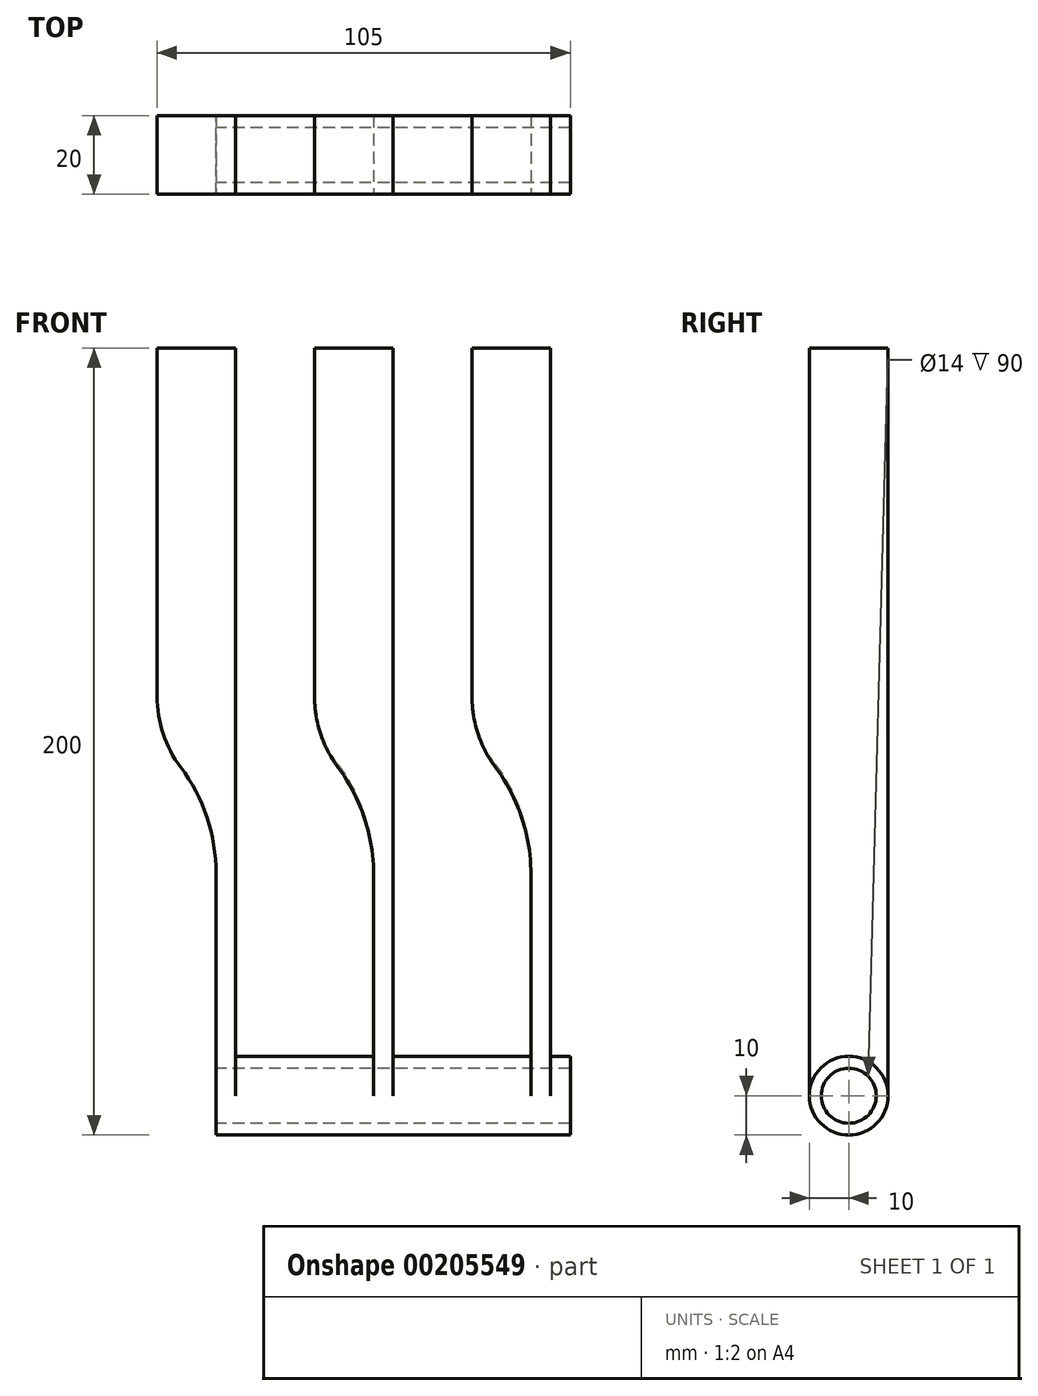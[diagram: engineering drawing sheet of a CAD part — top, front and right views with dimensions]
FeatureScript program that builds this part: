
annotation { "Feature Type Name" : "Feature", "Feature Type Description" : "" }
export const myFeature = defineFeature(function(context is Context, id is Id, definition is map)
    precondition{}
    {
        {
            assignVariable(context, id + "F0", {"name" : "width", "anyValue" : 120 * mm});
        }
        {
            var Q0;
            Q0=qCreatedBy(makeId("Front.planeOp"),FACE);
            var sketch = newSketch(context, id + "F1", { "sketchPlane" : qUnion([Q0])});
            skLineSegment(sketch, "E0.bottom", {"start": v(0, 0) * mm, "end": v(120, 0) * mm});
            skLineSegment(sketch, "E0.top", {"start": v(0, 200) * mm, "end": v(120, 200) * mm});
            skLineSegment(sketch, "E0.left", {"start": v(0, 0) * mm, "end": v(0, 200) * mm});
            skLineSegment(sketch, "E0.right", {"start": v(120, 0) * mm, "end": v(120, 200) * mm});
            skSolve(sketch);
        }
        {
            var Q0;
            Q0=qSketchRegion(id+"F1",true);
            extrude(context, id + "F2", {"entities" : qUnion([Q0]), "depth" : 1 / 6 * getVariable(context, 'width')});
        }
        {
            var Q0;
            Q0=makeQuery(id+"F2.opExtrude","SWEPT_FACE",FACE,{"disambiguationData":[OSD([sQuery(id+"F1.wireOp",EDGE,"E0.left")])]});
            var sketch = newSketch(context, id + "F3", { "sketchPlane" : qUnion([Q0])});
            skCircle(sketch, "E1", {"center": v(10, 10) * mm, "radius": 10 * mm});
            skPoint(sketch, "E1.centerSnap0", {"position": v(10, 0) * mm});
            skSolve(sketch);
        }
        {
            var Q0;
            {var subQ0=sQuery(id+"F3.wireOp",EDGE,"E1");var subQ1=sQuery(id+"F1.wireOp",EDGE,"E0.left");var subQ2=makeQuery(id+"F2.opExtrude","CAP_EDGE",EDGE,{"disambiguationData":[OSD([subQ1])],"isStart":false});var subQ3=makeQuery(id+"F3.imprint","INTERSECT",VERTEX,{"derivedFrom":[subQ2,subQ0]});Q0=makeQuery(id+"F3.imprint","IMPRINT",FACE,{"disambiguationData":[TD([[makeQuery(id+"F3.imprint","IMPRINT",EDGE,{"disambiguationData":[TD([[subQ3,1.0]])],"derivedFrom":subQ0}),-1.0]])]});}
            var Q1;
            {var subQ0=sQuery(id+"F3.wireOp",EDGE,"E1");var subQ1=sQuery(id+"F1.wireOp",EDGE,"E0.left");var subQ2=makeQuery(id+"F2.opExtrude","CAP_EDGE",EDGE,{"disambiguationData":[OSD([subQ1])],"isStart":true});var subQ3=makeQuery(id+"F3.imprint","INTERSECT",VERTEX,{"derivedFrom":[subQ2,subQ0]});Q1=makeQuery(id+"F3.imprint","IMPRINT",FACE,{"disambiguationData":[TD([[makeQuery(id+"F3.imprint","IMPRINT",EDGE,{"disambiguationData":[TD([[subQ3,-1.0]])],"derivedFrom":subQ0}),-1.0]])]});}
            var Q2;
            Q2=makeQuery(id+"F2.opExtrude","CAP_EDGE",EDGE,{"disambiguationData":[OSD([sQuery(id+"F1.wireOp",EDGE,"E0.bottom")])],"isStart":false});
            sweep(context, id + "F4", {"operationType" : NewBodyOperationType.REMOVE, "profiles" : qUnion([Q0, Q1]), "path" : qUnion([Q2])});
        }
        {
            var Q0;
            Q0=makeQuery(id+"F2.opExtrude","CAP_FACE",FACE,{"disambiguationData":[OSD([sQuery(id+"F1.wireOp",EDGE,"E0.bottom"),sQuery(id+"F1.wireOp",EDGE,"E0.top"),sQuery(id+"F1.wireOp",EDGE,"E0.left"),sQuery(id+"F1.wireOp",EDGE,"E0.right")])],"isStart":false});
            var sketch = newSketch(context, id + "F5", { "sketchPlane" : qUnion([Q0])});
            skLineSegment(sketch, "E2", {"start": v(60, 200) * mm, "end": v(60, 10) * mm});
            skLineSegment(sketch, "E3", {"start": v(20, 200) * mm, "end": v(20, 10) * mm});
            skLineSegment(sketch, "E4", {"start": v(40, 200) * mm, "end": v(40, 10) * mm});
            skLineSegment(sketch, "E5.MirrorCS", {"start": v(80, 200) * mm, "end": v(80, 10) * mm});
            skLineSegment(sketch, "E6.MirrorCS", {"start": v(100, 200) * mm, "end": v(100, 10) * mm});
            skSolve(sketch);
        }
        {
            var Q0;
            {var subQ0=sQuery(id+"F5.wireOp",EDGE,"E3");Q0=makeQuery(id+"F5.imprint","IMPRINT",FACE,{"disambiguationData":[TD([[makeQuery(id+"F5.imprint","IMPRINT",EDGE,{"derivedFrom":subQ0}),1.0]])]});}
            var Q1;
            {var subQ0=sQuery(id+"F5.wireOp",EDGE,"E2");Q1=makeQuery(id+"F5.imprint","IMPRINT",FACE,{"disambiguationData":[TD([[makeQuery(id+"F5.imprint","IMPRINT",EDGE,{"derivedFrom":subQ0}),1.0]])]});}
            var Q2;
            {var subQ0=sQuery(id+"F5.wireOp",EDGE,"E6.MirrorCS");Q2=makeQuery(id+"F5.imprint","IMPRINT",FACE,{"disambiguationData":[TD([[makeQuery(id+"F5.imprint","IMPRINT",EDGE,{"derivedFrom":subQ0}),1.0]])]});}
            var Q3;
            Q3=qConstructionFilter(qBodyType(qCreatedBy(id+"F3",EDGE),BodyType.WIRE),ConstructionObject.NO);
            sweep(context, id + "F6", {"operationType" : NewBodyOperationType.REMOVE, "profiles" : qUnion([Q0, Q1, Q2]), "path" : qUnion([Q3])});
        }
        {
            var Q0;
            Q0=makeQuery(id+"F2.opExtrude","SWEPT_FACE",FACE,{"disambiguationData":[OSD([sQuery(id+"F1.wireOp",EDGE,"E0.left")])]});
            var sketch = newSketch(context, id + "F7", { "sketchPlane" : qUnion([Q0])});
            skCircle(sketch, "E7", {"center": v(10, 10) * mm, "radius": 7 * mm});
            skSolve(sketch);
        }
        {
            var Q0;
            Q0=qSketchRegion(id+"F7",true);
            extrude(context, id + "F8", {"entities" : qUnion([Q0]), "operationType" : NewBodyOperationType.REMOVE, "endBound" : BoundingType.THROUGH_ALL, "oppositeDirection" : true, "depth" : 25 * mm});
        }
        {
            var Q0;
            Q0=qCreatedBy(makeId("Front.planeOp"),FACE);
            var sketch = newSketch(context, id + "F9", { "sketchPlane" : qUnion([Q0])});
            skLineSegment(sketch, "E8.bottom", {"start": v(0, 100) * mm, "end": v(15, 100) * mm});
            skLineSegment(sketch, "E8.top", {"start": v(0, 0) * mm, "end": v(15, 0) * mm});
            skLineSegment(sketch, "E8.left", {"start": v(0, 100) * mm, "end": v(0, 0) * mm});
            skLineSegment(sketch, "E8.right", {"start": v(15, 100) * mm, "end": v(15, 0) * mm});
            skSolve(sketch);
        }
        {
            var Q0;
            Q0=qSketchRegion(id+"F9",true);
            var Q1;
            Q1=makeQuery(id+"F2.opExtrude","SWEPT_EDGE",EDGE,{"disambiguationData":[OSD([sQuery(id+"F1.wireOp",EDGE,"E0.top"),sQuery(id+"F1.wireOp",EDGE,"E0.left")])]});
            sweep(context, id + "F10", {"operationType" : NewBodyOperationType.REMOVE, "profiles" : qUnion([Q0]), "path" : qUnion([Q1])});
        }
        {
            var Q0;
            Q0=qCreatedBy(makeId("Front.planeOp"),FACE);
            var sketch = newSketch(context, id + "F11", { "sketchPlane" : qUnion([Q0])});
            skLineSegment(sketch, "E9.bottom", {"start": v(40, 100) * mm, "end": v(55, 100) * mm});
            skLineSegment(sketch, "E9.top", {"start": v(40, 10) * mm, "end": v(55, 10) * mm});
            skLineSegment(sketch, "E9.left", {"start": v(40, 100) * mm, "end": v(40, 10) * mm});
            skLineSegment(sketch, "E9.right", {"start": v(55, 100) * mm, "end": v(55, 10) * mm});
            skLineSegment(sketch, "E10.bottom", {"start": v(80, 100) * mm, "end": v(95, 100) * mm});
            skLineSegment(sketch, "E10.top", {"start": v(80, 10) * mm, "end": v(95, 10) * mm});
            skLineSegment(sketch, "E10.left", {"start": v(80, 100) * mm, "end": v(80, 10) * mm});
            skLineSegment(sketch, "E10.right", {"start": v(95, 100) * mm, "end": v(95, 10) * mm});
            skSolve(sketch);
        }
        {
            var Q0;
            Q0=qSketchRegion(id+"F11",true);
            var Q1;
            Q1=makeQuery(id+"F6.boolean.opBoolean","COPY",EDGE,{"derivedFrom":makeQuery(id+"F6.opSweep","SWEPT_EDGE",EDGE,{"disambiguationData":[OSD([sQuery(id+"F1.wireOp",EDGE,"E0.bottom"),sQuery(id+"F1.wireOp",EDGE,"E0.left"),sQuery(id+"F3.wireOp",EDGE,"E1"),sQuery(id+"F5.wireOp",EDGE,"E4")])]})});
            sweep(context, id + "F12", {"operationType" : NewBodyOperationType.REMOVE, "profiles" : qUnion([Q0]), "path" : qUnion([Q1])});
        }
        {
            var Q0;
            Q0=makeQuery(id+"F10.boolean.opBoolean","COPY",EDGE,{"derivedFrom":makeQuery(id+"F10.opSweep","SWEPT_EDGE",EDGE,{"disambiguationData":[OSD([sQuery(id+"F1.wireOp",EDGE,"E0.top"),sQuery(id+"F1.wireOp",EDGE,"E0.left"),sQuery(id+"F9.wireOp",EDGE,"E8.bottom"),sQuery(id+"F9.wireOp",EDGE,"E8.right")])]})});
            var Q1;
            Q1=makeQuery(id+"F12.boolean.opBoolean","COPY",EDGE,{"derivedFrom":makeQuery(id+"F12.opSweep","SWEPT_EDGE",EDGE,{"disambiguationData":[OSD([sQuery(id+"F1.wireOp",EDGE,"E0.bottom"),sQuery(id+"F1.wireOp",EDGE,"E0.left"),sQuery(id+"F3.wireOp",EDGE,"E1"),sQuery(id+"F5.wireOp",EDGE,"E4"),sQuery(id+"F11.wireOp",EDGE,"E9.bottom"),sQuery(id+"F11.wireOp",EDGE,"E9.right")])]})});
            var Q2;
            Q2=makeQuery(id+"F12.boolean.opBoolean","COPY",EDGE,{"derivedFrom":makeQuery(id+"F12.opSweep","SWEPT_EDGE",EDGE,{"disambiguationData":[OSD([sQuery(id+"F1.wireOp",EDGE,"E0.bottom"),sQuery(id+"F1.wireOp",EDGE,"E0.left"),sQuery(id+"F3.wireOp",EDGE,"E1"),sQuery(id+"F5.wireOp",EDGE,"E4"),sQuery(id+"F11.wireOp",EDGE,"E10.bottom"),sQuery(id+"F11.wireOp",EDGE,"E10.right")])]})});
            fillet(context, id + "F13", {"entities" : qUnion([Q0, Q1, Q2]), "radius" : 45 * mm, "tangentPropagation" : true, "allowEdgeOverflow" : false});
        }
        {
            var Q0;
            {var subQ0=sQuery(id+"F1.wireOp",EDGE,"E0.left");Q0=makeQuery(id+"F13.opFillet","BLEND_EDGE",EDGE,{"blendedFrom":[makeQuery(id+"F10.boolean.opBoolean","COPY",EDGE,{"derivedFrom":makeQuery(id+"F10.opSweep","SWEPT_EDGE",EDGE,{"disambiguationData":[OSD([sQuery(id+"F1.wireOp",EDGE,"E0.top"),subQ0,sQuery(id+"F9.wireOp",EDGE,"E8.bottom"),sQuery(id+"F9.wireOp",EDGE,"E8.right")])]})}),makeQuery(id+"F2.opExtrude","SWEPT_FACE",FACE,{"disambiguationData":[OSD([subQ0])]})],"blendedInto":[makeQuery(id+"F2.opExtrude","SWEPT_FACE",FACE,{"disambiguationData":[OSD([subQ0])]})]});}
            var Q1;
            {var subQ0=sQuery(id+"F5.wireOp",EDGE,"E4");var subQ1=sQuery(id+"F3.wireOp",EDGE,"E1");Q1=makeQuery(id+"F13.opFillet","BLEND_EDGE",EDGE,{"blendedFrom":[makeQuery(id+"F12.boolean.opBoolean","COPY",EDGE,{"derivedFrom":makeQuery(id+"F12.opSweep","SWEPT_EDGE",EDGE,{"disambiguationData":[OSD([sQuery(id+"F1.wireOp",EDGE,"E0.bottom"),sQuery(id+"F1.wireOp",EDGE,"E0.left"),subQ1,subQ0,sQuery(id+"F11.wireOp",EDGE,"E9.bottom"),sQuery(id+"F11.wireOp",EDGE,"E9.right")])]})}),makeQuery(id+"F6.boolean.opBoolean","COPY",FACE,{"derivedFrom":makeQuery(id+"F6.opSweep","SWEPT_FACE",FACE,{"disambiguationData":[OSD([subQ1,subQ0])]})})],"blendedInto":[makeQuery(id+"F6.boolean.opBoolean","COPY",FACE,{"derivedFrom":makeQuery(id+"F6.opSweep","SWEPT_FACE",FACE,{"disambiguationData":[OSD([subQ1,subQ0])]})})]});}
            var Q2;
            {var subQ0=sQuery(id+"F3.wireOp",EDGE,"E1");Q2=makeQuery(id+"F13.opFillet","BLEND_EDGE",EDGE,{"blendedFrom":[makeQuery(id+"F12.boolean.opBoolean","COPY",EDGE,{"derivedFrom":makeQuery(id+"F12.opSweep","SWEPT_EDGE",EDGE,{"disambiguationData":[OSD([sQuery(id+"F1.wireOp",EDGE,"E0.bottom"),sQuery(id+"F1.wireOp",EDGE,"E0.left"),subQ0,sQuery(id+"F5.wireOp",EDGE,"E4"),sQuery(id+"F11.wireOp",EDGE,"E10.bottom"),sQuery(id+"F11.wireOp",EDGE,"E10.right")])]})}),makeQuery(id+"F6.boolean.opBoolean","COPY",FACE,{"derivedFrom":makeQuery(id+"F6.opSweep","SWEPT_FACE",FACE,{"disambiguationData":[OSD([subQ0,sQuery(id+"F5.wireOp",EDGE,"E5.MirrorCS")])]})})],"blendedInto":[makeQuery(id+"F6.boolean.opBoolean","COPY",FACE,{"derivedFrom":makeQuery(id+"F6.opSweep","SWEPT_FACE",FACE,{"disambiguationData":[OSD([subQ0,sQuery(id+"F5.wireOp",EDGE,"E5.MirrorCS")])]})})]});}
            fillet(context, id + "F14", {"entities" : qUnion([Q0, Q1, Q2]), "radius" : 30 * mm, "tangentPropagation" : true, "allowEdgeOverflow" : false});
        }
        {
            var Q0;
            Q0=qCreatedBy(makeId("Front.planeOp"),FACE);
            var sketch = newSketch(context, id + "F15", { "sketchPlane" : qUnion([Q0])});
            skLineSegment(sketch, "E11.bottom", {"start": v(105, 0) * mm, "end": v(120, 0) * mm});
            skLineSegment(sketch, "E11.top", {"start": v(105, 20) * mm, "end": v(120, 20) * mm});
            skLineSegment(sketch, "E11.left", {"start": v(105, 0) * mm, "end": v(105, 20) * mm});
            skLineSegment(sketch, "E11.right", {"start": v(120, 0) * mm, "end": v(120, 20) * mm});
            skSolve(sketch);
        }
        {
            var Q0;
            Q0=qSketchRegion(id+"F15",true);
            var Q1;
            Q1=makeQuery(id+"F6.boolean.opBoolean","INTERSECT",EDGE,{"derivedFrom":[makeQuery(id+"F2.opExtrude","SWEPT_FACE",FACE,{"disambiguationData":[OSD([sQuery(id+"F1.wireOp",EDGE,"E0.top")])]}),makeQuery(id+"F6.opSweep","SWEPT_FACE",FACE,{"disambiguationData":[OSD([sQuery(id+"F3.wireOp",EDGE,"E1"),sQuery(id+"F5.wireOp",EDGE,"E6.MirrorCS")])]})]});
            sweep(context, id + "F16", {"operationType" : NewBodyOperationType.REMOVE, "profiles" : qUnion([Q0]), "path" : qUnion([Q1])});
        }
    });
